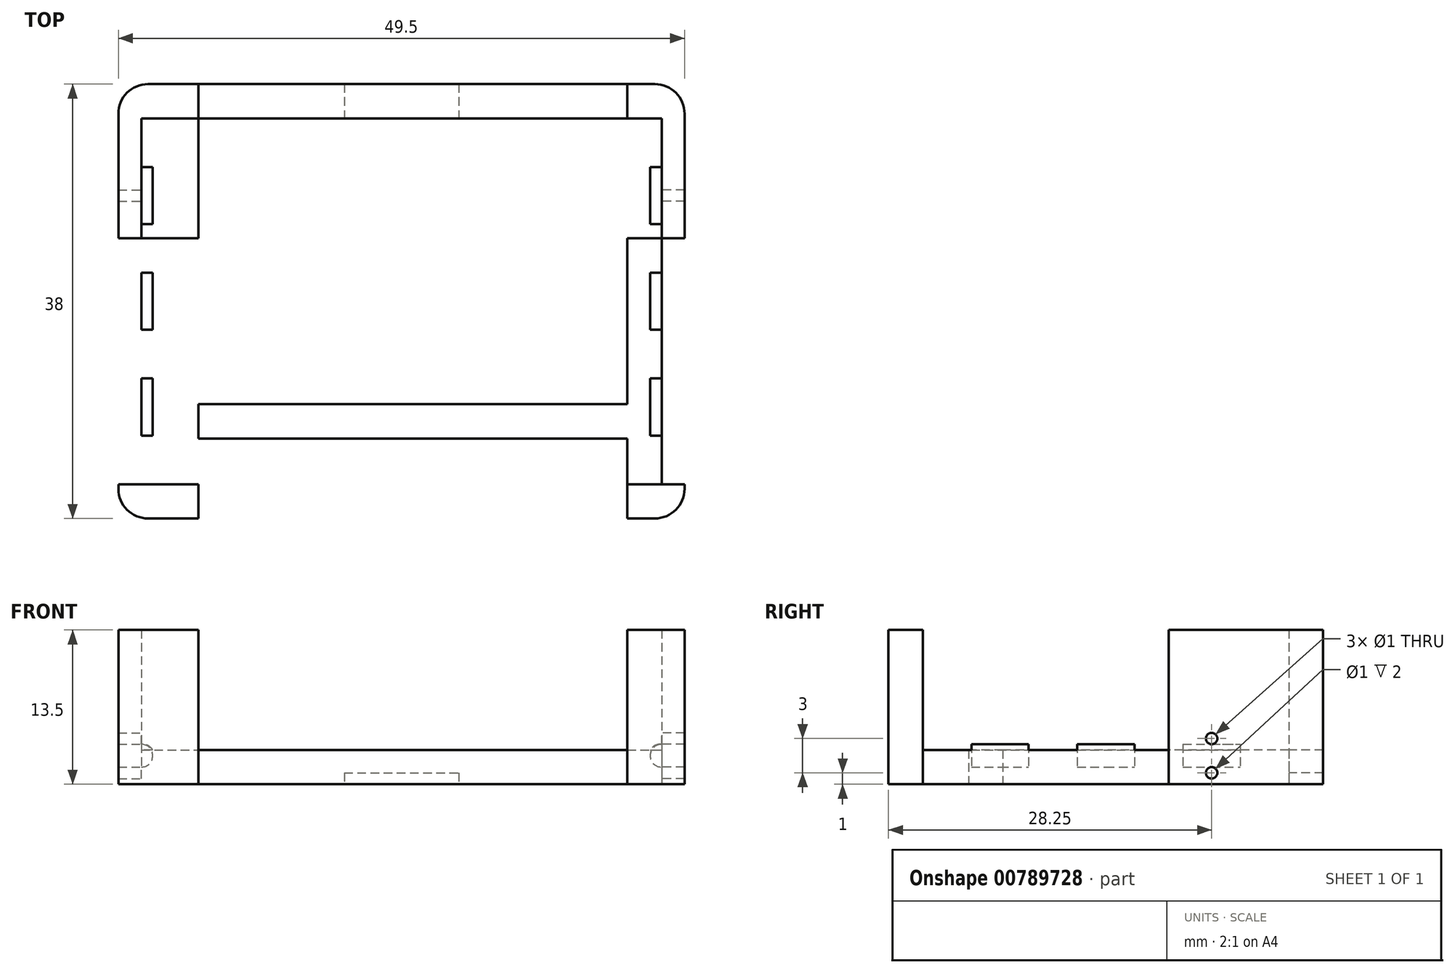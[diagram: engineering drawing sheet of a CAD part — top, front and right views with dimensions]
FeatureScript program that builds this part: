
annotation { "Feature Type Name" : "Feature", "Feature Type Description" : "" }
export const myFeature = defineFeature(function(context is Context, id is Id, definition is map)
    precondition{}
    {
        {
            var Q0;
            Q0=qCreatedBy(makeId("Top.planeOp"),FACE);
            var sketch = newSketch(context, id + "F0", { "sketchPlane" : qUnion([Q0])});
            skLineSegment(sketch, "E0.bottom", {"start": v(-24.75, 19) * mm, "end": v(24.75, 19) * mm});
            skLineSegment(sketch, "E0.top", {"start": v(-24.75, -19) * mm, "end": v(24.75, -19) * mm});
            skLineSegment(sketch, "E0.left", {"start": v(-24.75, 19) * mm, "end": v(-24.75, -19) * mm});
            skLineSegment(sketch, "E0.right", {"start": v(24.75, 19) * mm, "end": v(24.75, -19) * mm});
            skLineSegment(sketch, "E1.bottom", {"start": v(-24.75, 16) * mm, "end": v(24.75, 16) * mm});
            skLineSegment(sketch, "E1.top", {"start": v(-24.75, -16) * mm, "end": v(24.75, -16) * mm});
            skLineSegment(sketch, "E2", {"start": v(-22.75, 19) * mm, "end": v(-22.75, -19) * mm});
            skLineSegment(sketch, "E3", {"start": v(22.75, 19) * mm, "end": v(22.75, -19) * mm});
            skLineSegment(sketch, "E4", {"start": v(19.75, 19) * mm, "end": v(19.75, 16) * mm});
            skLineSegment(sketch, "E5", {"start": v(19.75, -16) * mm, "end": v(19.75, -19) * mm});
            skLineSegment(sketch, "E6", {"start": v(19.75, 16) * mm, "end": v(19.75, -16) * mm});
            skLineSegment(sketch, "E7", {"start": v(-17.75, 19) * mm, "end": v(-17.75, -19) * mm});
            skLineSegment(sketch, "E8", {"start": v(-17.75, -9) * mm, "end": v(19.75, -9) * mm});
            skLineSegment(sketch, "E9", {"start": v(-17.75, -12) * mm, "end": v(19.75, -12) * mm});
            skLineSegment(sketch, "E10", {"start": v(-24.75, 5.5) * mm, "end": v(29.75, 5.5) * mm});
            skLineSegment(sketch, "E11", {"start": v(29.75, 5.5) * mm, "end": v(29.75, 19) * mm});
            skLineSegment(sketch, "E12", {"start": v(29.75, 19) * mm, "end": v(24.75, 19) * mm});
            skSolve(sketch);
        }
        {
            var Q0;
            {var subQ0=sQuery(id+"F0.wireOp",EDGE,"E1.bottom");var subQ1=sQuery(id+"F0.wireOp",EDGE,"E0.left");var subQ2=makeQuery(id+"F0.imprint","INTERSECT",VERTEX,{"derivedFrom":[subQ1,subQ0]});Q0=makeQuery(id+"F0.imprint","IMPRINT",FACE,{"disambiguationData":[TD([[makeQuery(id+"F0.imprint","IMPRINT",EDGE,{"disambiguationData":[TD([[subQ2,-1.0]])],"derivedFrom":subQ1}),1.0]])]});}
            var Q1;
            {var subQ0=sQuery(id+"F0.wireOp",EDGE,"E0.left");var subQ1=sQuery(id+"F0.wireOp",EDGE,"E0.bottom");var subQ2=makeQuery(id+"F0.imprint","INTERSECT",VERTEX,{"derivedFrom":[subQ1,subQ0]});Q1=makeQuery(id+"F0.imprint","IMPRINT",FACE,{"disambiguationData":[TD([[makeQuery(id+"F0.imprint","IMPRINT",EDGE,{"disambiguationData":[TD([[subQ2,-1.0]])],"derivedFrom":subQ1}),-1.0]])]});}
            var Q2;
            {var subQ3=sQuery(id+"F0.wireOp",EDGE,"JlUuSNjJ-N2WR-d7uv-6GBG-oXMLz9WUw5uQ");Q2=makeQuery(id+"F0.imprint","IMPRINT",FACE,{"disambiguationData":[TD([[makeQuery(id+"F0.imprint","IMPRINT",EDGE,{"derivedFrom":subQ3}),-1.0]])]});}
            var Q3;
            {var subQ3=sQuery(id+"F0.wireOp",EDGE,"6ny0mRPX-NTV9-We4M-mDfU-sZ6HuERO2ziz");Q3=makeQuery(id+"F0.imprint","IMPRINT",FACE,{"disambiguationData":[TD([[makeQuery(id+"F0.imprint","IMPRINT",EDGE,{"derivedFrom":subQ3}),-1.0]])]});}
            var Q4;
            {var subQ0=sQuery(id+"F0.wireOp",EDGE,"E0.left");var subQ1=sQuery(id+"F0.wireOp",EDGE,"E0.top");var subQ2=makeQuery(id+"F0.imprint","INTERSECT",VERTEX,{"derivedFrom":[subQ1,subQ0]});Q4=makeQuery(id+"F0.imprint","IMPRINT",FACE,{"disambiguationData":[TD([[makeQuery(id+"F0.imprint","IMPRINT",EDGE,{"disambiguationData":[TD([[subQ2,-1.0]])],"derivedFrom":subQ1}),1.0]])]});}
            var Q5;
            {var subQ3=sQuery(id+"F0.wireOp",EDGE,"E5");Q5=makeQuery(id+"F0.imprint","IMPRINT",FACE,{"disambiguationData":[TD([[makeQuery(id+"F0.imprint","IMPRINT",EDGE,{"derivedFrom":subQ3}),1.0]])]});}
            var Q6;
            {var subQ0=sQuery(id+"F0.wireOp",EDGE,"E0.right");var subQ1=sQuery(id+"F0.wireOp",EDGE,"E0.top");var subQ2=makeQuery(id+"F0.imprint","INTERSECT",VERTEX,{"derivedFrom":[subQ1,subQ0]});Q6=makeQuery(id+"F0.imprint","IMPRINT",FACE,{"disambiguationData":[TD([[makeQuery(id+"F0.imprint","IMPRINT",EDGE,{"disambiguationData":[TD([[subQ2,1.0]])],"derivedFrom":subQ1}),1.0]])]});}
            var Q7;
            {var subQ0=sQuery(id+"F0.wireOp",EDGE,"E1.bottom");var subQ1=sQuery(id+"F0.wireOp",EDGE,"E0.right");var subQ2=makeQuery(id+"F0.imprint","INTERSECT",VERTEX,{"derivedFrom":[subQ1,subQ0]});Q7=makeQuery(id+"F0.imprint","IMPRINT",FACE,{"disambiguationData":[TD([[makeQuery(id+"F0.imprint","IMPRINT",EDGE,{"disambiguationData":[TD([[subQ2,-1.0]])],"derivedFrom":subQ1}),-1.0]])]});}
            var Q8;
            {var subQ0=sQuery(id+"F0.wireOp",EDGE,"E0.right");var subQ1=sQuery(id+"F0.wireOp",EDGE,"E0.bottom");var subQ2=makeQuery(id+"F0.imprint","INTERSECT",VERTEX,{"derivedFrom":[subQ1,subQ0]});Q8=makeQuery(id+"F0.imprint","IMPRINT",FACE,{"disambiguationData":[TD([[makeQuery(id+"F0.imprint","IMPRINT",EDGE,{"disambiguationData":[TD([[subQ2,1.0]])],"derivedFrom":subQ1}),-1.0]])]});}
            var Q9;
            {var subQ3=sQuery(id+"F0.wireOp",EDGE,"E4");Q9=makeQuery(id+"F0.imprint","IMPRINT",FACE,{"disambiguationData":[TD([[makeQuery(id+"F0.imprint","IMPRINT",EDGE,{"derivedFrom":subQ3}),1.0]])]});}
            var Q10;
            {var subQ0=sQuery(id+"F0.wireOp",EDGE,"E2");var subQ1=sQuery(id+"F0.wireOp",EDGE,"E0.bottom");var subQ2=makeQuery(id+"F0.imprint","INTERSECT",VERTEX,{"derivedFrom":[subQ1,subQ0]});Q10=makeQuery(id+"F0.imprint","IMPRINT",FACE,{"disambiguationData":[TD([[makeQuery(id+"F0.imprint","IMPRINT",EDGE,{"disambiguationData":[TD([[subQ2,-1.0]])],"derivedFrom":subQ1}),-1.0]])]});}
            var Q11;
            {var subQ0=sQuery(id+"F0.wireOp",EDGE,"E2");var subQ1=sQuery(id+"F0.wireOp",EDGE,"E0.top");var subQ2=makeQuery(id+"F0.imprint","INTERSECT",VERTEX,{"derivedFrom":[subQ1,subQ0]});Q11=makeQuery(id+"F0.imprint","IMPRINT",FACE,{"disambiguationData":[TD([[makeQuery(id+"F0.imprint","IMPRINT",EDGE,{"disambiguationData":[TD([[subQ2,-1.0]])],"derivedFrom":subQ1}),1.0]])]});}
            extrude(context, id + "F1", {"entities" : qUnion([Q0, Q1, Q2, Q3, Q4, Q5, Q6, Q7, Q8, Q9, Q10, Q11]), "depth" : 13.5 * mm, "offsetDistance" : 25 * mm});
        }
        {
            var Q0;
            {var subQ0=sQuery(id+"F0.wireOp",EDGE,"E4");Q0=makeQuery(id+"F0.imprint","IMPRINT",FACE,{"disambiguationData":[TD([[makeQuery(id+"F0.imprint","IMPRINT",EDGE,{"derivedFrom":subQ0}),-1.0]])]});}
            var Q1;
            {var subQ0=sQuery(id+"F0.wireOp",EDGE,"E2");var subQ1=sQuery(id+"F0.wireOp",EDGE,"E1.bottom");var subQ2=makeQuery(id+"F0.imprint","INTERSECT",VERTEX,{"derivedFrom":[subQ1,subQ0]});Q1=makeQuery(id+"F0.imprint","IMPRINT",FACE,{"disambiguationData":[TD([[makeQuery(id+"F0.imprint","IMPRINT",EDGE,{"disambiguationData":[TD([[subQ2,-1.0]])],"derivedFrom":subQ1}),-1.0]])]});}
            var Q2;
            {var subQ0=sQuery(id+"F0.wireOp",EDGE,"E6");Q2=makeQuery(id+"F0.imprint","IMPRINT",FACE,{"disambiguationData":[TD([[makeQuery(id+"F0.imprint","IMPRINT",EDGE,{"derivedFrom":subQ0}),1.0]])]});}
            var Q3;
            {var subQ0=sQuery(id+"F0.wireOp",EDGE,"E8");Q3=makeQuery(id+"F0.imprint","IMPRINT",FACE,{"disambiguationData":[TD([[makeQuery(id+"F0.imprint","IMPRINT",EDGE,{"derivedFrom":subQ0}),-1.0]])]});}
            extrude(context, id + "F2", {"entities" : qUnion([Q0, Q1, Q2, Q3]), "depth" : 3 * mm, "offsetDistance" : 25 * mm});
        }
        {
            var Q0;
            Q0=makeQuery(id+"F1.opExtrude","SWEPT_EDGE",EDGE,{"disambiguationData":[OSD([sQuery(id+"F0.wireOp",EDGE,"E0.bottom"),sQuery(id+"F0.wireOp",EDGE,"E0.left")])]});
            var Q1;
            Q1=makeQuery(id+"F1.opExtrude","SWEPT_EDGE",EDGE,{"disambiguationData":[OSD([sQuery(id+"F0.wireOp",EDGE,"E0.bottom"),sQuery(id+"F0.wireOp",EDGE,"E0.right")])]});
            var Q2;
            Q2=makeQuery(id+"F1.opExtrude","SWEPT_EDGE",EDGE,{"disambiguationData":[OSD([sQuery(id+"F0.wireOp",EDGE,"E0.top"),sQuery(id+"F0.wireOp",EDGE,"E0.right")])]});
            var Q3;
            Q3=makeQuery(id+"F1.opExtrude","SWEPT_EDGE",EDGE,{"disambiguationData":[OSD([sQuery(id+"F0.wireOp",EDGE,"E0.top"),sQuery(id+"F0.wireOp",EDGE,"E0.left")])]});
            fillet(context, id + "F3", {"entities" : qUnion([Q0, Q1, Q2, Q3]), "radius" : 2.6 * mm, "tangentPropagation" : true, "allowEdgeOverflow" : false});
        }
        {
            var Q0;
            Q0=makeQuery(id+"F1.opExtrude","CAP_EDGE",EDGE,{"disambiguationData":[OSD([sQuery(id+"F0.wireOp",EDGE,"E3")])],"isStart":false});
            cPlane(context, id + "F4", {"entities" : qUnion([Q0]), "cplaneType" : CPlaneType.LINE_ANGLE, "offset" : 25 * mm, "angle" : 90 * degree, "width" : 150 * mm, "height" : 150 * mm});
        }
        {
            var Q0;
            Q0=qCreatedBy(id+"F4.planeOp",FACE);
            var sketch = newSketch(context, id + "F5", { "sketchPlane" : qUnion([Q0])});
            skLineSegment(sketch, "E13.bottom", {"start": v(-16, 13.5) * mm, "end": v(16, 13.5) * mm});
            skLineSegment(sketch, "E13.top", {"start": v(-16, -8.5) * mm, "end": v(16, -8.5) * mm});
            skLineSegment(sketch, "E13.left", {"start": v(-16, 13.5) * mm, "end": v(-16, -8.5) * mm});
            skLineSegment(sketch, "E13.right", {"start": v(16, 13.5) * mm, "end": v(16, -8.5) * mm});
            skLineSegment(sketch, "E14.bottom", {"start": v(-11.75, 1.5) * mm, "end": v(-6.75, 1.5) * mm});
            skLineSegment(sketch, "E14.top", {"start": v(-11.75, 3.5) * mm, "end": v(-6.75, 3.5) * mm});
            skLineSegment(sketch, "E14.left", {"start": v(-11.75, 3.5) * mm, "end": v(-11.75, 1.5) * mm});
            skLineSegment(sketch, "E14.right", {"start": v(-6.75, 3.5) * mm, "end": v(-6.75, 1.5) * mm});
            skLineSegment(sketch, "E15.bottom", {"start": v(-2.5, 1.5) * mm, "end": v(2.5, 1.5) * mm});
            skLineSegment(sketch, "E15.top", {"start": v(-2.5, 3.5) * mm, "end": v(2.5, 3.5) * mm});
            skLineSegment(sketch, "E15.left", {"start": v(-2.5, 3.5) * mm, "end": v(-2.5, 1.5) * mm});
            skLineSegment(sketch, "E15.right", {"start": v(2.5, 3.5) * mm, "end": v(2.5, 1.5) * mm});
            skLineSegment(sketch, "E16.bottom", {"start": v(6.75, 1.5) * mm, "end": v(11.75, 1.5) * mm});
            skLineSegment(sketch, "E16.top", {"start": v(6.75, 3.5) * mm, "end": v(11.75, 3.5) * mm});
            skLineSegment(sketch, "E16.left", {"start": v(6.75, 3.5) * mm, "end": v(6.75, 1.5) * mm});
            skLineSegment(sketch, "E16.right", {"start": v(11.75, 3.5) * mm, "end": v(11.75, 1.5) * mm});
            skLineSegment(sketch, "E17", {"start": v(11.75, 2.5) * mm, "end": v(16, 2.5) * mm, "construction": true});
            skLineSegment(sketch, "E18", {"start": v(-11.75, 2.5) * mm, "end": v(-16, 2.5) * mm, "construction": true});
            skLineSegment(sketch, "E19", {"start": v(-6.75, 2.5) * mm, "end": v(-2.5, 2.5) * mm, "construction": true});
            skLineSegment(sketch, "E20", {"start": v(2.5, 2.5) * mm, "end": v(6.75, 2.5) * mm, "construction": true});
            skCircle(sketch, "E21", {"center": v(-9.25, 4) * mm, "radius": 0.5 * mm});
            skPoint(sketch, "E21.centerSnap0", {"position": v(-9.25, 3.5) * mm});
            skCircle(sketch, "E22", {"center": v(0, 4) * mm, "radius": 0.5 * mm});
            skPoint(sketch, "E22.centerSnap0", {"position": v(0, 3.5) * mm});
            skCircle(sketch, "E23", {"center": v(9.25, 4) * mm, "radius": 0.5 * mm});
            skPoint(sketch, "E23.centerSnap0", {"position": v(9.25, 3.5) * mm});
            skCircle(sketch, "E24", {"center": v(-9.25, 1) * mm, "radius": 0.5 * mm});
            skPoint(sketch, "E24.centerSnap0", {"position": v(-9.25, 1.5) * mm});
            skCircle(sketch, "E25", {"center": v(0, 1) * mm, "radius": 0.5 * mm});
            skPoint(sketch, "E25.centerSnap0", {"position": v(0, 1.5) * mm});
            skCircle(sketch, "E26", {"center": v(9.25, 1) * mm, "radius": 0.5 * mm});
            skPoint(sketch, "E26.centerSnap0", {"position": v(9.25, 1.5) * mm});
            skSolve(sketch);
        }
        {
            var Q0;
            Q0=makeQuery(id+"F5.imprint","IMPRINT",FACE,{"disambiguationData":[TD([[makeQuery(id+"F5.imprint","IMPRINT",EDGE,{"derivedFrom":sQuery(id+"F5.wireOp",EDGE,"E14.bottom")}),1.0]])]});
            var Q1;
            Q1=makeQuery(id+"F5.imprint","IMPRINT",FACE,{"disambiguationData":[TD([[makeQuery(id+"F5.imprint","IMPRINT",EDGE,{"derivedFrom":sQuery(id+"F5.wireOp",EDGE,"E15.bottom")}),1.0]])]});
            var Q2;
            Q2=makeQuery(id+"F5.imprint","IMPRINT",FACE,{"disambiguationData":[TD([[makeQuery(id+"F5.imprint","IMPRINT",EDGE,{"derivedFrom":sQuery(id+"F5.wireOp",EDGE,"E16.bottom")}),1.0]])]});
            extrude(context, id + "F6", {"entities" : qUnion([Q0, Q1, Q2]), "operationType" : NewBodyOperationType.ADD, "oppositeDirection" : true, "depth" : 1 * mm, "offsetDistance" : 25 * mm});
        }
        {
            var Q0;
            Q0=makeQuery(id+"F6.opExtrude","CAP_EDGE",EDGE,{"disambiguationData":[OSD([sQuery(id+"F5.wireOp",EDGE,"E14.top")])],"isStart":false});
            var Q1;
            Q1=makeQuery(id+"F6.opExtrude","CAP_EDGE",EDGE,{"disambiguationData":[OSD([sQuery(id+"F5.wireOp",EDGE,"E14.bottom")])],"isStart":false});
            var Q2;
            Q2=makeQuery(id+"F6.opExtrude","CAP_EDGE",EDGE,{"disambiguationData":[OSD([sQuery(id+"F5.wireOp",EDGE,"E15.top")])],"isStart":false});
            var Q3;
            Q3=makeQuery(id+"F6.opExtrude","CAP_EDGE",EDGE,{"disambiguationData":[OSD([sQuery(id+"F5.wireOp",EDGE,"E15.bottom")])],"isStart":false});
            var Q4;
            Q4=makeQuery(id+"F6.opExtrude","CAP_EDGE",EDGE,{"disambiguationData":[OSD([sQuery(id+"F5.wireOp",EDGE,"E16.bottom")])],"isStart":false});
            var Q5;
            Q5=makeQuery(id+"F6.opExtrude","CAP_EDGE",EDGE,{"disambiguationData":[OSD([sQuery(id+"F5.wireOp",EDGE,"E16.top")])],"isStart":false});
            fillet(context, id + "F7", {"entities" : qUnion([Q0, Q1, Q2, Q3, Q4, Q5]), "radius" : 1 * mm, "tangentPropagation" : true, "allowEdgeOverflow" : false});
        }
        {
            var Q0;
            Q0=makeQuery(id+"F1.opExtrude","CAP_EDGE",EDGE,{"disambiguationData":[OSD([sQuery(id+"F0.wireOp",EDGE,"E2")])],"isStart":false});
            cPlane(context, id + "F8", {"entities" : qUnion([Q0]), "cplaneType" : CPlaneType.LINE_ANGLE, "offset" : 25 * mm, "angle" : 90 * degree, "width" : 150 * mm, "height" : 150 * mm});
        }
        {
            var Q0;
            Q0=qCreatedBy(id+"F8.planeOp",FACE);
            var sketch = newSketch(context, id + "F9", { "sketchPlane" : qUnion([Q0])});
            skLineSegment(sketch, "E27.bottom", {"start": v(-16, 13.5) * mm, "end": v(16, 13.5) * mm});
            skLineSegment(sketch, "E27.top", {"start": v(-16, -8.5) * mm, "end": v(16, -8.5) * mm});
            skLineSegment(sketch, "E27.left", {"start": v(-16, 13.5) * mm, "end": v(-16, -8.5) * mm});
            skLineSegment(sketch, "E27.right", {"start": v(16, 13.5) * mm, "end": v(16, -8.5) * mm});
            skLineSegment(sketch, "E28.bottom", {"start": v(-11.75, 1.5) * mm, "end": v(-6.75, 1.5) * mm});
            skLineSegment(sketch, "E28.top", {"start": v(-11.75, 3.5) * mm, "end": v(-6.75, 3.5) * mm});
            skLineSegment(sketch, "E28.left", {"start": v(-11.75, 3.5) * mm, "end": v(-11.75, 1.5) * mm});
            skLineSegment(sketch, "E28.right", {"start": v(-6.75, 3.5) * mm, "end": v(-6.75, 1.5) * mm});
            skLineSegment(sketch, "E29.bottom", {"start": v(-2.5, 1.5) * mm, "end": v(2.5, 1.5) * mm});
            skLineSegment(sketch, "E29.top", {"start": v(-2.5, 3.5) * mm, "end": v(2.5, 3.5) * mm});
            skLineSegment(sketch, "E29.left", {"start": v(-2.5, 3.5) * mm, "end": v(-2.5, 1.5) * mm});
            skLineSegment(sketch, "E29.right", {"start": v(2.5, 3.5) * mm, "end": v(2.5, 1.5) * mm});
            skLineSegment(sketch, "E30.bottom", {"start": v(6.75, 1.5) * mm, "end": v(11.75, 1.5) * mm});
            skLineSegment(sketch, "E30.top", {"start": v(6.75, 3.5) * mm, "end": v(11.75, 3.5) * mm});
            skLineSegment(sketch, "E30.left", {"start": v(6.75, 3.5) * mm, "end": v(6.75, 1.5) * mm});
            skLineSegment(sketch, "E30.right", {"start": v(11.75, 3.5) * mm, "end": v(11.75, 1.5) * mm});
            skLineSegment(sketch, "E31", {"start": v(11.75, 2.5) * mm, "end": v(16, 2.5) * mm, "construction": true});
            skLineSegment(sketch, "E32", {"start": v(-11.75, 2.5) * mm, "end": v(-16, 2.5) * mm, "construction": true});
            skLineSegment(sketch, "E33", {"start": v(-6.75, 2.5) * mm, "end": v(-2.5, 2.5) * mm, "construction": true});
            skLineSegment(sketch, "E34", {"start": v(2.5, 2.5) * mm, "end": v(6.75, 2.5) * mm, "construction": true});
            skCircle(sketch, "E35", {"center": v(9.25, 4) * mm, "radius": 0.5 * mm});
            skPoint(sketch, "E35.centerSnap0", {"position": v(9.25, 3.5) * mm});
            skCircle(sketch, "E36", {"center": v(0, 4) * mm, "radius": 0.5 * mm});
            skCircle(sketch, "E37", {"center": v(-9.25, 4) * mm, "radius": 0.5 * mm});
            skPoint(sketch, "E37.centerSnap0", {"position": v(-9.25, 3.5) * mm});
            skCircle(sketch, "E38", {"center": v(-9.25, 1) * mm, "radius": 0.5 * mm});
            skPoint(sketch, "E38.centerSnap0", {"position": v(-9.25, 1.5) * mm});
            skCircle(sketch, "E39", {"center": v(0, 1) * mm, "radius": 0.5 * mm});
            skPoint(sketch, "E39.centerSnap0", {"position": v(0, 1.5) * mm});
            skCircle(sketch, "E40", {"center": v(9.25, 1) * mm, "radius": 0.5 * mm});
            skPoint(sketch, "E40.centerSnap0", {"position": v(9.25, 1.5) * mm});
            skSolve(sketch);
        }
        {
            var Q0;
            Q0=makeQuery(id+"F9.imprint","IMPRINT",FACE,{"disambiguationData":[TD([[makeQuery(id+"F9.imprint","IMPRINT",EDGE,{"derivedFrom":sQuery(id+"F9.wireOp",EDGE,"E28.bottom")}),1.0]])]});
            var Q1;
            Q1=makeQuery(id+"F9.imprint","IMPRINT",FACE,{"disambiguationData":[TD([[makeQuery(id+"F9.imprint","IMPRINT",EDGE,{"derivedFrom":sQuery(id+"F9.wireOp",EDGE,"E29.bottom")}),1.0]])]});
            var Q2;
            Q2=makeQuery(id+"F9.imprint","IMPRINT",FACE,{"disambiguationData":[TD([[makeQuery(id+"F9.imprint","IMPRINT",EDGE,{"derivedFrom":sQuery(id+"F9.wireOp",EDGE,"E30.bottom")}),1.0]])]});
            extrude(context, id + "F10", {"entities" : qUnion([Q0, Q1, Q2]), "operationType" : NewBodyOperationType.ADD, "depth" : 1 * mm, "offsetDistance" : 25 * mm});
        }
        {
            var Q0;
            Q0=makeQuery(id+"F10.opExtrude","CAP_EDGE",EDGE,{"disambiguationData":[OSD([sQuery(id+"F9.wireOp",EDGE,"E28.top")])],"isStart":false});
            var Q1;
            Q1=makeQuery(id+"F10.opExtrude","CAP_EDGE",EDGE,{"disambiguationData":[OSD([sQuery(id+"F9.wireOp",EDGE,"E28.bottom")])],"isStart":false});
            var Q2;
            Q2=makeQuery(id+"F10.opExtrude","CAP_EDGE",EDGE,{"disambiguationData":[OSD([sQuery(id+"F9.wireOp",EDGE,"E29.top")])],"isStart":false});
            var Q3;
            Q3=makeQuery(id+"F10.opExtrude","CAP_EDGE",EDGE,{"disambiguationData":[OSD([sQuery(id+"F9.wireOp",EDGE,"E30.top")])],"isStart":false});
            var Q4;
            Q4=makeQuery(id+"F10.opExtrude","CAP_EDGE",EDGE,{"disambiguationData":[OSD([sQuery(id+"F9.wireOp",EDGE,"E29.bottom")])],"isStart":false});
            var Q5;
            Q5=makeQuery(id+"F10.opExtrude","CAP_EDGE",EDGE,{"disambiguationData":[OSD([sQuery(id+"F9.wireOp",EDGE,"E30.bottom")])],"isStart":false});
            fillet(context, id + "F11", {"entities" : qUnion([Q0, Q1, Q2, Q3, Q4, Q5]), "radius" : 1 * mm, "tangentPropagation" : true, "allowEdgeOverflow" : false});
        }
        {
            var Q0;
            Q0=makeQuery(id+"F5.imprint","IMPRINT",FACE,{"disambiguationData":[TD([[makeQuery(id+"F5.imprint","IMPRINT",EDGE,{"derivedFrom":sQuery(id+"F5.wireOp",EDGE,"E21")}),1.0]])]});
            var Q1;
            Q1=makeQuery(id+"F5.imprint","IMPRINT",FACE,{"disambiguationData":[TD([[makeQuery(id+"F5.imprint","IMPRINT",EDGE,{"derivedFrom":sQuery(id+"F5.wireOp",EDGE,"E22")}),1.0]])]});
            var Q2;
            Q2=makeQuery(id+"F5.imprint","IMPRINT",FACE,{"disambiguationData":[TD([[makeQuery(id+"F5.imprint","IMPRINT",EDGE,{"derivedFrom":sQuery(id+"F5.wireOp",EDGE,"E23")}),1.0]])]});
            var Q3;
            Q3=makeQuery(id+"F5.imprint","IMPRINT",FACE,{"disambiguationData":[TD([[makeQuery(id+"F5.imprint","IMPRINT",EDGE,{"derivedFrom":sQuery(id+"F5.wireOp",EDGE,"E26")}),1.0]])]});
            var Q4;
            Q4=makeQuery(id+"F5.imprint","IMPRINT",FACE,{"disambiguationData":[TD([[makeQuery(id+"F5.imprint","IMPRINT",EDGE,{"derivedFrom":sQuery(id+"F5.wireOp",EDGE,"E25")}),1.0]])]});
            var Q5;
            Q5=makeQuery(id+"F5.imprint","IMPRINT",FACE,{"disambiguationData":[TD([[makeQuery(id+"F5.imprint","IMPRINT",EDGE,{"derivedFrom":sQuery(id+"F5.wireOp",EDGE,"E24")}),1.0]])]});
            extrude(context, id + "F12", {"entities" : qUnion([Q0, Q1, Q2, Q3, Q4, Q5]), "operationType" : NewBodyOperationType.REMOVE, "depth" : 5 * mm, "offsetDistance" : 25 * mm});
        }
        {
            var Q0;
            Q0=makeQuery(id+"F9.imprint","IMPRINT",FACE,{"disambiguationData":[TD([[makeQuery(id+"F9.imprint","IMPRINT",EDGE,{"derivedFrom":sQuery(id+"F9.wireOp",EDGE,"E37")}),1.0]])]});
            var Q1;
            Q1=makeQuery(id+"F9.imprint","IMPRINT",FACE,{"disambiguationData":[TD([[makeQuery(id+"F9.imprint","IMPRINT",EDGE,{"derivedFrom":sQuery(id+"F9.wireOp",EDGE,"E36")}),1.0]])]});
            var Q2;
            Q2=makeQuery(id+"F9.imprint","IMPRINT",FACE,{"disambiguationData":[TD([[makeQuery(id+"F9.imprint","IMPRINT",EDGE,{"derivedFrom":sQuery(id+"F9.wireOp",EDGE,"E35")}),1.0]])]});
            var Q3;
            Q3=makeQuery(id+"F9.imprint","IMPRINT",FACE,{"disambiguationData":[TD([[makeQuery(id+"F9.imprint","IMPRINT",EDGE,{"derivedFrom":sQuery(id+"F9.wireOp",EDGE,"E40")}),1.0]])]});
            var Q4;
            Q4=makeQuery(id+"F9.imprint","IMPRINT",FACE,{"disambiguationData":[TD([[makeQuery(id+"F9.imprint","IMPRINT",EDGE,{"derivedFrom":sQuery(id+"F9.wireOp",EDGE,"E39")}),1.0]])]});
            var Q5;
            Q5=makeQuery(id+"F9.imprint","IMPRINT",FACE,{"disambiguationData":[TD([[makeQuery(id+"F9.imprint","IMPRINT",EDGE,{"derivedFrom":sQuery(id+"F9.wireOp",EDGE,"E38")}),1.0]])]});
            extrude(context, id + "F13", {"entities" : qUnion([Q0, Q1, Q2, Q3, Q4, Q5]), "operationType" : NewBodyOperationType.REMOVE, "oppositeDirection" : true, "depth" : 5 * mm, "offsetDistance" : 25 * mm});
        }
        {
            var Q0;
            Q0=qCreatedBy(makeId("Front.planeOp"),FACE);
            var sketch = newSketch(context, id + "F14", { "sketchPlane" : qUnion([Q0])});
            skLineSegment(sketch, "E41.bottom", {"start": v(5, 0) * mm, "end": v(-5, 0) * mm});
            skLineSegment(sketch, "E41.top", {"start": v(5, 1) * mm, "end": v(-5, 1) * mm});
            skLineSegment(sketch, "E41.left", {"start": v(5, 0) * mm, "end": v(5, 1) * mm});
            skLineSegment(sketch, "E41.right", {"start": v(-5, 0) * mm, "end": v(-5, 1) * mm});
            skSolve(sketch);
        }
        {
            var Q0;
            Q0=makeQuery(id+"F14.imprint","IMPRINT",FACE,{"disambiguationData":[TD([[makeQuery(id+"F14.imprint","IMPRINT",EDGE,{"derivedFrom":sQuery(id+"F14.wireOp",EDGE,"E41.bottom")}),-1.0]])]});
            extrude(context, id + "F15", {"entities" : qUnion([Q0]), "operationType" : NewBodyOperationType.REMOVE, "oppositeDirection" : true, "depth" : 25 * mm, "offsetDistance" : 25 * mm});
        }
    });
